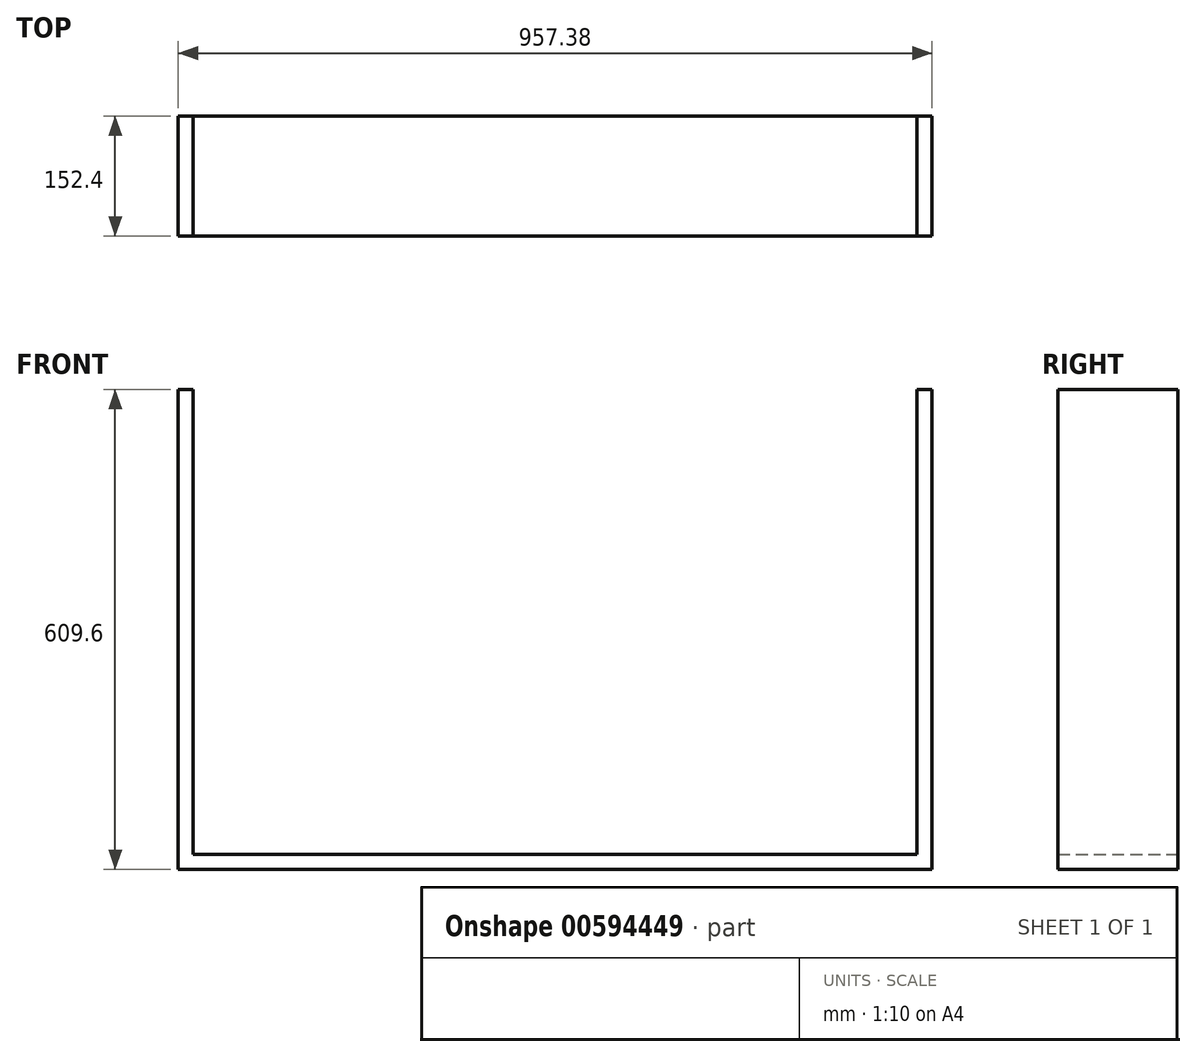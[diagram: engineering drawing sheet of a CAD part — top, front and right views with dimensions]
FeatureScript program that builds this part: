
annotation { "Feature Type Name" : "Feature", "Feature Type Description" : "" }
export const myFeature = defineFeature(function(context is Context, id is Id, definition is map)
    precondition{}
    {
        {
            var Q0;
            Q0=qCreatedBy(makeId("Front.planeOp"),FACE);
            var sketch = newSketch(context, id + "F0", { "sketchPlane" : qUnion([Q0])});
            skLineSegment(sketch, "E0.bottom", {"start": v(0, 0) * mm, "end": v(19.05, 0) * mm});
            skLineSegment(sketch, "E0.top", {"start": v(0, 609.6) * mm, "end": v(19.05, 609.6) * mm});
            skLineSegment(sketch, "E0.left", {"start": v(0, 0) * mm, "end": v(0, 609.6) * mm});
            skLineSegment(sketch, "E0.right", {"start": v(19.05, 0) * mm, "end": v(19.05, 609.6) * mm});
            skLineSegment(sketch, "E1.bottom", {"start": v(19.05, 19.05) * mm, "end": v(938.33, 19.05) * mm});
            skLineSegment(sketch, "E1.top", {"start": v(19.05, 0) * mm, "end": v(938.33, 0) * mm});
            skLineSegment(sketch, "E1.left", {"start": v(19.05, 19.05) * mm, "end": v(19.05, 0) * mm});
            skLineSegment(sketch, "E1.right", {"start": v(938.33, 19.05) * mm, "end": v(938.33, 0) * mm});
            skLineSegment(sketch, "E2.bottom", {"start": v(938.33, 0) * mm, "end": v(957.38, 0) * mm});
            skLineSegment(sketch, "E2.top", {"start": v(938.33, 609.6) * mm, "end": v(957.38, 609.6) * mm});
            skLineSegment(sketch, "E2.left", {"start": v(938.33, 0) * mm, "end": v(938.33, 609.6) * mm});
            skLineSegment(sketch, "E2.right", {"start": v(957.38, 0) * mm, "end": v(957.38, 609.6) * mm});
            skSolve(sketch);
        }
        {
            var Q0;
            {var subQ3=sQuery(id+"F0.wireOp",EDGE,"E2.bottom");Q0=makeQuery(id+"F0.imprint","IMPRINT",FACE,{"disambiguationData":[TD([[makeQuery(id+"F0.imprint","IMPRINT",EDGE,{"derivedFrom":subQ3}),1.0]])]});}
            extrude(context, id + "F1", {"entities" : qUnion([Q0]), "depth" : 152.4 * mm, "offsetDistance" : 25.4 * mm});
        }
        {
            var Q0;
            {var subQ0=sQuery(id+"F0.wireOp",EDGE,"E1.bottom");Q0=makeQuery(id+"F0.imprint","IMPRINT",FACE,{"disambiguationData":[TD([[makeQuery(id+"F0.imprint","IMPRINT",EDGE,{"derivedFrom":subQ0}),-1.0]])]});}
            var Q1;
            Q1=makeQuery(id+"F1.opExtrude","CAP_FACE",FACE,{"disambiguationData":[OSD([sQuery(id+"F0.wireOp",EDGE,"E2.bottom"),sQuery(id+"F0.wireOp",EDGE,"E2.top"),sQuery(id+"F0.wireOp",EDGE,"E2.left"),sQuery(id+"F0.wireOp",EDGE,"E2.right")])],"isStart":false});
            extrude(context, id + "F2", {"entities" : qUnion([Q0]), "operationType" : NewBodyOperationType.ADD, "endBound" : BoundingType.UP_TO_SURFACE, "depth" : 25.4 * mm, "endBoundEntityFace" : qUnion([Q1]), "offsetDistance" : 25.4 * mm});
        }
        {
            var Q0;
            Q0=makeQuery(id+"F0.imprint","IMPRINT",FACE,{"disambiguationData":[TD([[makeQuery(id+"F0.imprint","IMPRINT",EDGE,{"derivedFrom":sQuery(id+"F0.wireOp",EDGE,"E0.bottom")}),1.0]])]});
            var Q1;
            {var subQ0=sQuery(id+"F0.wireOp",EDGE,"E2.right");var subQ1=sQuery(id+"F0.wireOp",EDGE,"E2.left");var subQ2=sQuery(id+"F0.wireOp",EDGE,"E2.top");var subQ3=sQuery(id+"F0.wireOp",EDGE,"E2.bottom");Q1=makeQuery(id+"F2.boolean.opBoolean","MERGE",FACE,{"derivedFrom":[makeQuery(id+"F1.opExtrude","CAP_FACE",FACE,{"disambiguationData":[OSD([subQ3,subQ2,subQ1,subQ0])],"isStart":false}),makeQuery(id+"F2.opExtrude","CAP_FACE",FACE,{"disambiguationData":[OSD([subQ3,subQ2,subQ1,subQ0])],"isStart":false})]});}
            extrude(context, id + "F3", {"entities" : qUnion([Q0]), "operationType" : NewBodyOperationType.ADD, "endBound" : BoundingType.UP_TO_SURFACE, "depth" : 25.4 * mm, "endBoundEntityFace" : qUnion([Q1]), "offsetDistance" : 25.4 * mm});
        }
    });
